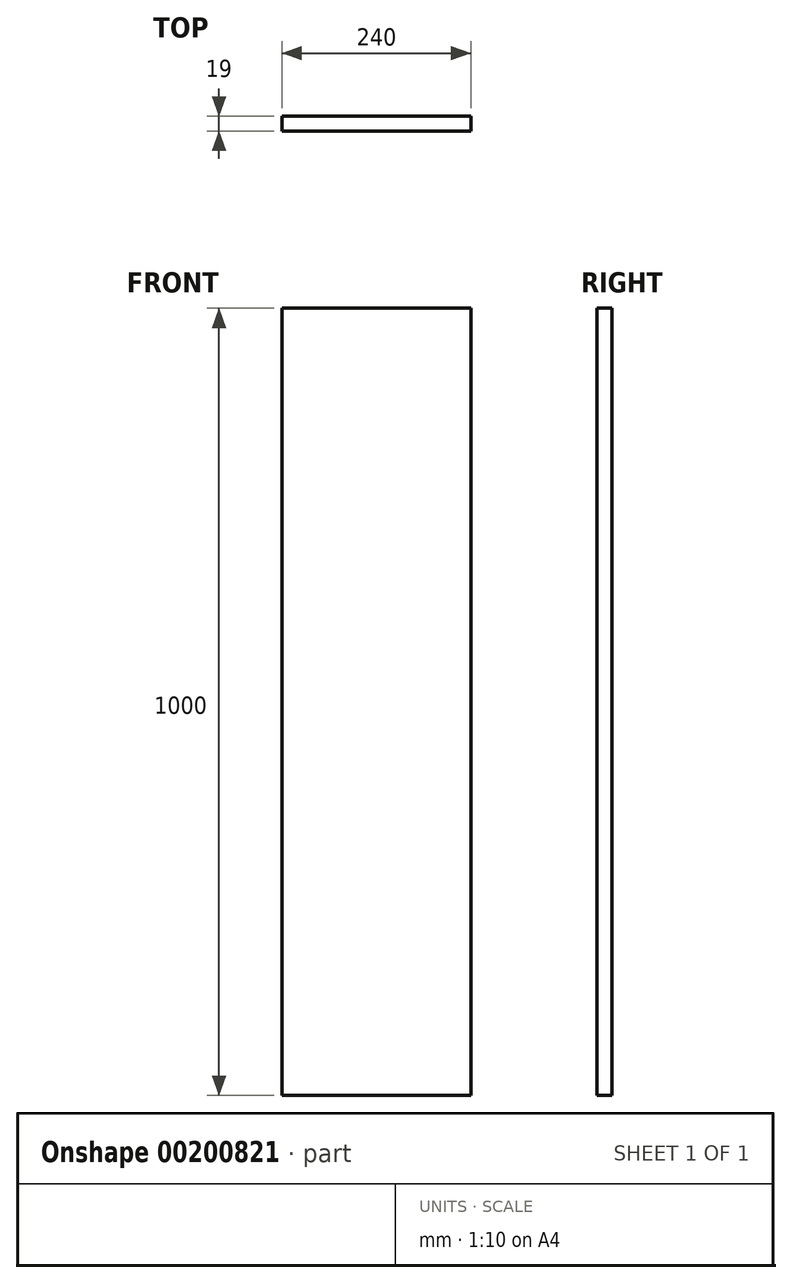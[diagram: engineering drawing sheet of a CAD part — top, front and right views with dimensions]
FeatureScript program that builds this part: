
annotation { "Feature Type Name" : "Feature", "Feature Type Description" : "" }
export const myFeature = defineFeature(function(context is Context, id is Id, definition is map)
    precondition{}
    {
        {
            var Q0;
            Q0=qCreatedBy(makeId("Front.planeOp"),FACE);
            var sketch = newSketch(context, id + "F0", { "sketchPlane" : qUnion([Q0])});
            skLineSegment(sketch, "E0.bottom", {"start": v(-119.36, 742.56) * mm, "end": v(120.64, 742.56) * mm});
            skLineSegment(sketch, "E0.top", {"start": v(-119.36, -257.44) * mm, "end": v(120.64, -257.44) * mm});
            skLineSegment(sketch, "E0.left", {"start": v(-119.36, 742.56) * mm, "end": v(-119.36, -257.44) * mm});
            skLineSegment(sketch, "E0.right", {"start": v(120.64, 742.56) * mm, "end": v(120.64, -257.44) * mm});
            skSolve(sketch);
        }
        {
            var Q0;
            Q0=makeQuery(id+"F0.imprint","IMPRINT",FACE,{"disambiguationData":[TD([[makeQuery(id+"F0.imprint","IMPRINT",EDGE,{"derivedFrom":sQuery(id+"F0.wireOp",EDGE,"E0.bottom")}),-1.0]])]});
            extrude(context, id + "F1", {"entities" : qUnion([Q0]), "depth" : 19 * mm});
        }
    });
